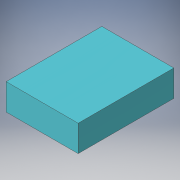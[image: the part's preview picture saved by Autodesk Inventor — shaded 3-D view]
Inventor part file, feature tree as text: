
AUTODESK INVENTOR PART (.ipt)
format: ipt  version: 2016 (Build 200138000, 138)  size: 88,064 bytes
history: native  units: in
note: dims shown in document units (in); Inventor stores cm internally (conversion verified against a paired STEP export)
features: extrude x1, sketch x1
ambient origin geometry x8: Origin, YZ Plane, XZ Plane, XY Plane, X Axis, Y Axis, Z Axis, Center Point
bodies: Solid1 (feature_tree)
feature tree (2):
  extrude  "Extrusion1"  Depth=0.93in
  sketch  "Sketch1"  dims[d0=0.7in d1=0.93in d2=0.256in d3=0.0in]
